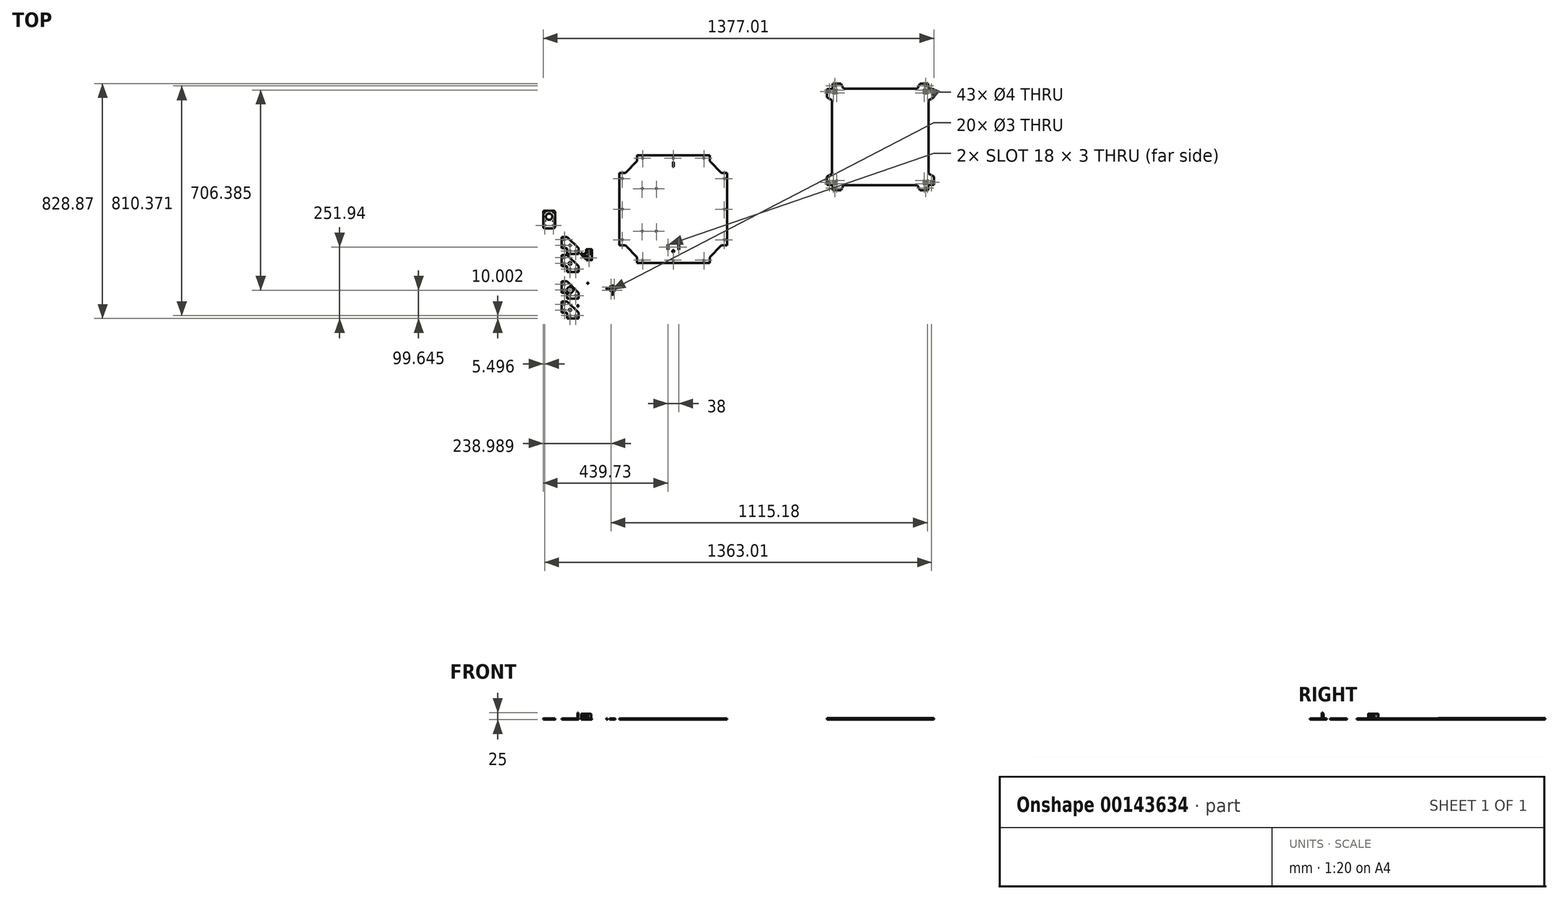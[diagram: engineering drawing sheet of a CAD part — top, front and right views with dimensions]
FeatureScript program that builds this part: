
annotation { "Feature Type Name" : "Feature", "Feature Type Description" : "" }
export const myFeature = defineFeature(function(context is Context, id is Id, definition is map)
    precondition{}
    {
        {
            var Q0;
            Q0=qCreatedBy(makeId("Top.planeOp"),FACE);
            var sketch = newSketch(context, id + "F0", { "sketchPlane" : qUnion([Q0])});
            skLineSegment(sketch, "E0.left", {"start": v(-190, 128) * mm, "end": v(-190, -128) * mm});
            skPoint(sketch, "E0.middle", {"position": v(0, 0) * mm});
            skLineSegment(sketch, "E1", {"start": v(-190, 0) * mm, "end": v(-137.24, 0) * mm, "construction": true});
            skLineSegment(sketch, "E2", {"start": v(0, -170) * mm, "end": v(0, -128) * mm, "construction": true});
            skPoint(sketch, "E3.middle", {"position": v(0, -149) * mm});
            skLineSegment(sketch, "E4", {"start": v(-180, -128) * mm, "end": v(-180, 128) * mm, "construction": true});
            skLineSegment(sketch, "E5", {"start": v(-147, 180) * mm, "end": v(23, 180) * mm, "construction": true});
            skCircle(sketch, "E6", {"center": v(-180, 108) * mm, "radius": 2 * mm});
            skLineSegment(sketch, "E7", {"start": v(23, 180) * mm, "end": v(193, 180) * mm, "construction": true});
            skCircle(sketch, "E8", {"center": v(108, 180) * mm, "radius": 2 * mm});
            skCircle(sketch, "E9.MirrorC", {"center": v(108, -180) * mm, "radius": 2 * mm});
            skLineSegment(sketch, "E10.bottom", {"start": v(-109.57, -77.46) * mm, "end": v(-59.57, -77.46) * mm, "construction": true});
            skLineSegment(sketch, "E10.top", {"start": v(-109.57, 72.54) * mm, "end": v(-59.57, 72.54) * mm, "construction": true});
            skLineSegment(sketch, "E10.left", {"start": v(-109.57, -77.46) * mm, "end": v(-109.57, 72.54) * mm, "construction": true});
            skLineSegment(sketch, "E10.right", {"start": v(-59.57, -77.46) * mm, "end": v(-59.57, 72.54) * mm, "construction": true});
            skCircle(sketch, "E11", {"center": v(-109.57, -77.46) * mm, "radius": 2 * mm});
            skCircle(sketch, "E12", {"center": v(-109.57, 72.54) * mm, "radius": 2 * mm});
            skCircle(sketch, "E13", {"center": v(-59.57, 72.54) * mm, "radius": 2 * mm});
            skCircle(sketch, "E14", {"center": v(-59.57, -77.46) * mm, "radius": 2 * mm});
            skCircle(sketch, "E15", {"center": v(0, -149) * mm, "radius": 3 * mm});
            skLineSegment(sketch, "E16", {"start": v(-373.83, -201.14) * mm, "end": v(-333.84, -161.15) * mm, "construction": true});
            skCircle(sketch, "E17", {"center": v(-363.83, -191.14) * mm, "radius": 11 * mm, "construction": true});
            skCircle(sketch, "E18", {"center": v(-363.83, -191.14) * mm, "radius": 5 * mm});
            skLineSegment(sketch, "E19", {"start": v(-373.83, -181.14) * mm, "end": v(-373.83, -161.14) * mm, "construction": true});
            skPoint(sketch, "E20", {"position": v(-333.83, -201.14) * mm});
            skLineSegment(sketch, "E21", {"start": v(-373.83, -161.14) * mm, "end": v(-393.83, -161.14) * mm});
            skLineSegment(sketch, "E22", {"start": v(-373.83, -161.14) * mm, "end": v(-333.83, -201.14) * mm});
            skLineSegment(sketch, "E23", {"start": v(-383.83, -181.14) * mm, "end": v(-393.83, -181.14) * mm});
            skLineSegment(sketch, "E24", {"start": v(-393.83, -181.14) * mm, "end": v(-373.83, -181.14) * mm});
            skLineSegment(sketch, "E25", {"start": v(-353.83, -201.14) * mm, "end": v(-353.83, -221.14) * mm});
            skLineSegment(sketch, "E26", {"start": v(-393.83, -161.14) * mm, "end": v(-373.83, -181.14) * mm, "construction": true});
            skLineSegment(sketch, "E27", {"start": v(-353.83, -201.14) * mm, "end": v(-333.83, -221.14) * mm, "construction": true});
            skCircle(sketch, "E28", {"center": v(-343.83, -211.14) * mm, "radius": 2 * mm});
            skCircle(sketch, "E29", {"center": v(-383.83, -171.14) * mm, "radius": 2 * mm});
            skCircle(sketch, "E30", {"center": v(-363.83, -191.14) * mm, "radius": 2.5 * mm});
            skLineSegment(sketch, "E31", {"start": v(-333.83, -201.14) * mm, "end": v(-333.83, -221.14) * mm});
            skLineSegment(sketch, "E32", {"start": v(-393.83, -181.14) * mm, "end": v(-393.83, -161.14) * mm});
            skLineSegment(sketch, "E33", {"start": v(-353.83, -221.14) * mm, "end": v(-333.83, -221.14) * mm});
            skLineSegment(sketch, "E34", {"start": v(-373.83, -181.14) * mm, "end": v(-353.83, -201.14) * mm, "construction": true});
            skPoint(sketch, "E35.orphan", {"position": v(-393.82, -221.12) * mm});
            skLineSegment(sketch, "E36", {"start": v(-393.83, -181.14) * mm, "end": v(-393.83, -201.14) * mm});
            skLineSegment(sketch, "E37", {"start": v(-393.83, -201.14) * mm, "end": v(-373.83, -201.14) * mm});
            skLineSegment(sketch, "E38", {"start": v(-373.83, -221.14) * mm, "end": v(-373.83, -201.14) * mm});
            skLineSegment(sketch, "E39", {"start": v(-373.83, -221.14) * mm, "end": v(-353.83, -221.14) * mm});
            skCircle(sketch, "E40.MirrorC", {"center": v(-363.83, -211.14) * mm, "radius": 2 * mm});
            skCircle(sketch, "E41.MirrorC", {"center": v(-383.83, -191.14) * mm, "radius": 2 * mm});
            skCircle(sketch, "E42", {"center": v(-280.98, -260.83) * mm, "radius": 11 * mm, "construction": true});
            skCircle(sketch, "E43", {"center": v(-280.98, -260.83) * mm, "radius": 2.75 * mm});
            skPoint(sketch, "E44", {"position": v(-250.98, -270.83) * mm});
            skLineSegment(sketch, "E45", {"start": v(-300.98, -250.83) * mm, "end": v(-310.98, -250.83) * mm});
            skLineSegment(sketch, "E46", {"start": v(-310.98, -250.83) * mm, "end": v(-270.98, -250.83) * mm});
            skLineSegment(sketch, "E47", {"start": v(-270.98, -250.83) * mm, "end": v(-270.98, -290.83) * mm});
            skLineSegment(sketch, "E48", {"start": v(-290.98, -250.83) * mm, "end": v(-290.98, -270.83) * mm});
            skArc(sketch, "E49", {"start": v(-280.98, -268.83) * mm, "mid": v(-275.33, -255.17) * mm, "end": v(-288.98, -260.83) * mm});
            skLineSegment(sketch, "E50", {"start": v(-290.98, -250.83) * mm, "end": v(-270.98, -270.83) * mm, "construction": true});
            skLineSegment(sketch, "E51", {"start": v(-310.98, -250.83) * mm, "end": v(-310.98, -270.83) * mm});
            skLineSegment(sketch, "E52", {"start": v(-310.98, -270.83) * mm, "end": v(-303.38, -270.83) * mm});
            skLineSegment(sketch, "E53", {"start": v(-290.98, -290.83) * mm, "end": v(-270.98, -290.83) * mm});
            skCircle(sketch, "E54.MirrorC", {"center": v(-280.98, -280.83) * mm, "radius": 2 * mm});
            skCircle(sketch, "E55.MirrorC", {"center": v(-300.98, -260.83) * mm, "radius": 2 * mm});
            skCircle(sketch, "E56.cCircle", {"center": v(-280.98, -260.83) * mm, "radius": 4.75 * mm, "construction": true});
            skLineSegment(sketch, "E56.0", {"start": v(-280.98, -256.08) * mm, "end": v(-276.87, -258.46) * mm});
            skLineSegment(sketch, "E56.1", {"start": v(-276.87, -258.46) * mm, "end": v(-276.87, -263.2) * mm});
            skLineSegment(sketch, "E56.2", {"start": v(-276.87, -263.2) * mm, "end": v(-280.98, -265.58) * mm});
            skLineSegment(sketch, "E56.3", {"start": v(-280.98, -265.58) * mm, "end": v(-285.1, -263.2) * mm});
            skLineSegment(sketch, "E56.4", {"start": v(-285.1, -263.2) * mm, "end": v(-285.1, -258.46) * mm});
            skLineSegment(sketch, "E56.5", {"start": v(-285.1, -258.46) * mm, "end": v(-280.98, -256.08) * mm});
            skLineSegment(sketch, "E57.top", {"start": v(-296.51, -264.83) * mm, "end": v(-292.98, -264.83) * mm});
            skLineSegment(sketch, "E58.left", {"start": v(-284.98, -290.83) * mm, "end": v(-284.98, -283.08) * mm});
            skPoint(sketch, "E59.orphan", {"position": v(-298.73, -264.83) * mm});
            skPoint(sketch, "E60.orphan", {"position": v(-303.23, -264.83) * mm});
            skPoint(sketch, "E61.orphan", {"position": v(-284.98, -278.58) * mm});
            skPoint(sketch, "E62.orphan", {"position": v(-284.98, -283.08) * mm});
            skPoint(sketch, "E63.visualSharp", {"position": v(-287.91, -264.83) * mm});
            skArc(sketch, "E63.filletArc", {"start": v(-292.98, -264.83) * mm, "mid": v(-290.15, -263.66) * mm, "end": v(-288.98, -260.83) * mm});
            skPoint(sketch, "E64.visualSharp", {"position": v(-284.98, -267.76) * mm});
            skArc(sketch, "E64.filletArc", {"start": v(-280.98, -268.83) * mm, "mid": v(-283.81, -270) * mm, "end": v(-284.98, -272.83) * mm});
            skArc(sketch, "E65", {"start": v(-305.46, -264.83) * mm, "mid": v(-300.98, -266.83) * mm, "end": v(-296.51, -264.83) * mm});
            skArc(sketch, "E66", {"start": v(-284.98, -276.36) * mm, "mid": v(-286.98, -280.83) * mm, "end": v(-284.98, -285.3) * mm});
            skLineSegment(sketch, "E67.trimOffspring", {"start": v(-284.98, -278.58) * mm, "end": v(-284.98, -272.83) * mm});
            skLineSegment(sketch, "E68.trimOffspring", {"start": v(-303.23, -264.83) * mm, "end": v(-310.98, -264.83) * mm});
            skLineSegment(sketch, "E69.bottom", {"start": v(559.78, 444.93) * mm, "end": v(899.78, 444.93) * mm});
            skLineSegment(sketch, "E69.top", {"start": v(559.78, 64.93) * mm, "end": v(899.78, 64.93) * mm});
            skLineSegment(sketch, "E69.left", {"start": v(539.78, 424.93) * mm, "end": v(539.78, 84.93) * mm});
            skLineSegment(sketch, "E69.right", {"start": v(919.78, 424.93) * mm, "end": v(919.78, 84.93) * mm});
            skPoint(sketch, "E69.middle", {"position": v(729.78, 254.93) * mm});
            skLineSegment(sketch, "E70.top", {"start": v(539.78, 84.93) * mm, "end": v(559.78, 84.93) * mm});
            skLineSegment(sketch, "E70.right", {"start": v(559.78, 64.93) * mm, "end": v(559.78, 84.93) * mm});
            skLineSegment(sketch, "E71", {"start": v(592.54, 254.93) * mm, "end": v(729.78, 64.93) * mm, "construction": true});
            skLineSegment(sketch, "E72", {"start": v(729.78, 64.93) * mm, "end": v(729.78, 254.93) * mm, "construction": true});
            skLineSegment(sketch, "E73.MirrorCS", {"start": v(559.78, 444.93) * mm, "end": v(559.78, 424.93) * mm});
            skLineSegment(sketch, "E74.MirrorCS", {"start": v(539.78, 424.93) * mm, "end": v(559.78, 424.93) * mm});
            skLineSegment(sketch, "E75.MirrorCS", {"start": v(899.78, 444.93) * mm, "end": v(899.78, 424.93) * mm});
            skLineSegment(sketch, "E76.MirrorCS", {"start": v(919.78, 424.93) * mm, "end": v(899.78, 424.93) * mm});
            skLineSegment(sketch, "E77.MirrorCS", {"start": v(899.78, 64.93) * mm, "end": v(899.78, 84.93) * mm});
            skLineSegment(sketch, "E78.MirrorCS", {"start": v(919.78, 84.93) * mm, "end": v(899.78, 84.93) * mm});
            skLineSegment(sketch, "E79", {"start": v(559.78, 84.93) * mm, "end": v(899.78, 84.93) * mm, "construction": true});
            skLineSegment(sketch, "E80", {"start": v(549.78, 424.93) * mm, "end": v(559.78, 434.93) * mm, "construction": true});
            skLineSegment(sketch, "E81", {"start": v(559.78, 434.93) * mm, "end": v(729.78, 434.93) * mm, "construction": true});
            skLineSegment(sketch, "E82", {"start": v(539.78, 64.93) * mm, "end": v(599.78, 124.93) * mm, "construction": true});
            skCircle(sketch, "E83", {"center": v(569.78, 94.93) * mm, "radius": 11 * mm, "construction": true});
            skCircle(sketch, "E84", {"center": v(569.78, 94.93) * mm, "radius": 4 * mm});
            skCircle(sketch, "E85.MirrorC", {"center": v(569.78, 414.93) * mm, "radius": 2.5 * mm});
            skCircle(sketch, "E86.MirrorC", {"center": v(889.78, 94.93) * mm, "radius": 4 * mm});
            skCircle(sketch, "E87.MirrorC", {"center": v(889.78, 414.93) * mm, "radius": 2.5 * mm});
            skLineSegment(sketch, "E88", {"start": v(559.78, 84.93) * mm, "end": v(559.78, 104.93) * mm, "construction": true});
            skPoint(sketch, "E89", {"position": v(599.78, 84.93) * mm});
            skLineSegment(sketch, "E90", {"start": v(549.78, 104.93) * mm, "end": v(539.78, 104.93) * mm});
            skLineSegment(sketch, "E91", {"start": v(559.78, 84.93) * mm, "end": v(579.78, 84.93) * mm});
            skLineSegment(sketch, "E92", {"start": v(579.78, 84.93) * mm, "end": v(579.78, 64.93) * mm, "construction": true});
            skLineSegment(sketch, "E93", {"start": v(559.78, 104.93) * mm, "end": v(559.78, 84.93) * mm});
            skLineSegment(sketch, "E94", {"start": v(539.78, 124.93) * mm, "end": v(559.78, 104.93) * mm, "construction": true});
            skLineSegment(sketch, "E95", {"start": v(579.78, 84.93) * mm, "end": v(599.78, 64.93) * mm, "construction": true});
            skCircle(sketch, "E96", {"center": v(569.78, 94.93) * mm, "radius": 8 * mm, "construction": true});
            skLineSegment(sketch, "E97", {"start": v(559.78, 104.93) * mm, "end": v(579.78, 84.93) * mm, "construction": true});
            skCircle(sketch, "E98.MirrorC", {"center": v(569.78, 74.93) * mm, "radius": 2 * mm});
            skCircle(sketch, "E99.MirrorC", {"center": v(549.78, 94.93) * mm, "radius": 2 * mm});
            skLineSegment(sketch, "E100", {"start": v(729.78, 254.93) * mm, "end": v(460.72, 254.93) * mm, "construction": true});
            skCircle(sketch, "E101.MirrorC", {"center": v(889.78, 74.93) * mm, "radius": 2 * mm});
            skCircle(sketch, "E102.MirrorC", {"center": v(909.78, 94.93) * mm, "radius": 2 * mm});
            skPoint(sketch, "E103.orphan", {"position": v(539.78, 444.93) * mm});
            skPoint(sketch, "E104.end.orphan", {"position": v(899.78, 434.93) * mm});
            skPoint(sketch, "E105.orphan", {"position": v(919.78, 64.93) * mm});
            skCircle(sketch, "E106.MirrorC", {"center": v(549.78, 414.93) * mm, "radius": 2 * mm});
            skCircle(sketch, "E107.MirrorC", {"center": v(569.78, 434.93) * mm, "radius": 2 * mm});
            skCircle(sketch, "E108.MirrorC", {"center": v(889.78, 434.93) * mm, "radius": 2 * mm});
            skCircle(sketch, "E109.MirrorC", {"center": v(909.78, 414.93) * mm, "radius": 2 * mm});
            skLineSegment(sketch, "E110", {"start": v(-290.98, -270.83) * mm, "end": v(-290.98, -278.43) * mm});
            skLineSegment(sketch, "E111.right", {"start": v(-298.58, -270.83) * mm, "end": v(-298.58, -272.67) * mm});
            skLineSegment(sketch, "E112.MirrorCS", {"start": v(-303.38, -270.83) * mm, "end": v(-303.38, -272.67) * mm});
            skLineSegment(sketch, "E113.bottom", {"start": v(-298.58, -272.67) * mm, "end": v(-297.48, -272.67) * mm});
            skLineSegment(sketch, "E113.right", {"start": v(-297.48, -272.67) * mm, "end": v(-297.48, -275.17) * mm});
            skLineSegment(sketch, "E114.MirrorCS", {"start": v(-304.48, -272.67) * mm, "end": v(-304.48, -275.17) * mm});
            skLineSegment(sketch, "E115.MirrorCS", {"start": v(-303.38, -272.67) * mm, "end": v(-304.48, -272.67) * mm});
            skArc(sketch, "E116", {"start": v(-304.48, -275.17) * mm, "mid": v(-300.98, -275.94) * mm, "end": v(-297.48, -275.17) * mm});
            skLineSegment(sketch, "E117.trimOffspring", {"start": v(-298.58, -270.83) * mm, "end": v(-290.98, -270.83) * mm});
            skPoint(sketch, "E111.bottom.start.orphan", {"position": v(-300.98, -270.83) * mm});
            skLineSegment(sketch, "E118.1.0", {"start": v(-292.82, -237.33) * mm, "end": v(-295.32, -237.33) * mm});
            skLineSegment(sketch, "E118.1.1", {"start": v(-292.82, -244.33) * mm, "end": v(-295.32, -244.33) * mm});
            skLineSegment(sketch, "E118.1.2", {"start": v(-290.98, -238.43) * mm, "end": v(-292.82, -238.43) * mm});
            skArc(sketch, "E118.1.3", {"start": v(-295.32, -237.33) * mm, "mid": v(-296.09, -240.83) * mm, "end": v(-295.32, -244.33) * mm});
            skLineSegment(sketch, "E118.1.4", {"start": v(-290.98, -230.83) * mm, "end": v(-290.98, -238.43) * mm});
            skLineSegment(sketch, "E118.1.5", {"start": v(-290.98, -243.23) * mm, "end": v(-292.82, -243.23) * mm});
            skLineSegment(sketch, "E118.1.6", {"start": v(-292.82, -243.23) * mm, "end": v(-292.82, -244.33) * mm});
            skLineSegment(sketch, "E118.1.7", {"start": v(-292.82, -238.43) * mm, "end": v(-292.82, -237.33) * mm});
            skLineSegment(sketch, "E118.1.8", {"start": v(-290.98, -243.23) * mm, "end": v(-290.98, -250.83) * mm});
            skLineSegment(sketch, "E118.anchor1", {"start": v(-280.98, -260.83) * mm, "end": v(-310.98, -270.83) * mm, "construction": true});
            skLineSegment(sketch, "E118.anchor2", {"start": v(-280.98, -260.83) * mm, "end": v(-290.98, -230.83) * mm, "construction": true});
            skLineSegment(sketch, "E119", {"start": v(-280.98, -260.83) * mm, "end": v(-319.58, -260.83) * mm, "construction": true});
            skPoint(sketch, "E119.endSnap0", {"position": v(-310.98, -260.83) * mm});
            skArc(sketch, "E120.MirrorCS", {"start": v(-295.32, -284.33) * mm, "mid": v(-296.09, -280.83) * mm, "end": v(-295.32, -277.33) * mm});
            skLineSegment(sketch, "E121.MirrorCS", {"start": v(-292.82, -284.33) * mm, "end": v(-295.32, -284.33) * mm});
            skLineSegment(sketch, "E122.MirrorCS", {"start": v(-290.98, -283.23) * mm, "end": v(-292.82, -283.23) * mm});
            skLineSegment(sketch, "E123.MirrorCS", {"start": v(-290.98, -278.43) * mm, "end": v(-292.82, -278.43) * mm});
            skLineSegment(sketch, "E124.MirrorCS", {"start": v(-292.82, -277.33) * mm, "end": v(-295.32, -277.33) * mm});
            skLineSegment(sketch, "E125.MirrorCS", {"start": v(-292.82, -278.43) * mm, "end": v(-292.82, -277.33) * mm});
            skLineSegment(sketch, "E126.MirrorCS", {"start": v(-292.82, -283.23) * mm, "end": v(-292.82, -284.33) * mm});
            skLineSegment(sketch, "E127.trimOffspring", {"start": v(-290.98, -283.23) * mm, "end": v(-290.98, -290.83) * mm});
            skLineSegment(sketch, "E128.0", {"start": v(-297.78, -272.97) * mm, "end": v(-297.78, -275.17) * mm});
            skLineSegment(sketch, "E128.1", {"start": v(-298.88, -272.97) * mm, "end": v(-297.78, -272.97) * mm});
            skLineSegment(sketch, "E128.2", {"start": v(-298.88, -270.83) * mm, "end": v(-298.88, -272.97) * mm});
            skLineSegment(sketch, "E129", {"start": v(-300.98, -270.83) * mm, "end": v(-300.98, -275.04) * mm, "construction": true});
            skLineSegment(sketch, "E130.MirrorCS", {"start": v(-304.18, -272.97) * mm, "end": v(-304.18, -275.17) * mm});
            skLineSegment(sketch, "E131.MirrorCS", {"start": v(-303.08, -270.83) * mm, "end": v(-303.08, -272.97) * mm});
            skLineSegment(sketch, "E132.MirrorCS", {"start": v(-303.08, -272.97) * mm, "end": v(-304.18, -272.97) * mm});
            skArc(sketch, "E133", {"start": v(-304.18, -275.17) * mm, "mid": v(-300.98, -275.98) * mm, "end": v(-297.78, -275.17) * mm});
            skLineSegment(sketch, "E134", {"start": v(-303.38, -270.83) * mm, "end": v(-303.08, -270.83) * mm});
            skLineSegment(sketch, "E135", {"start": v(-298.88, -270.83) * mm, "end": v(-298.58, -270.83) * mm});
            skLineSegment(sketch, "E136", {"start": v(-280.98, -280.83) * mm, "end": v(-291.9, -280.83) * mm, "construction": true});
            skPoint(sketch, "E136.endSnap0", {"position": v(-291.9, -283.23) * mm});
            skLineSegment(sketch, "E137.0", {"start": v(-293.12, -277.63) * mm, "end": v(-295.32, -277.63) * mm});
            skLineSegment(sketch, "E137.1", {"start": v(-293.12, -278.73) * mm, "end": v(-293.12, -277.63) * mm});
            skLineSegment(sketch, "E137.2", {"start": v(-290.98, -278.73) * mm, "end": v(-293.12, -278.73) * mm});
            skLineSegment(sketch, "E138.MirrorCS", {"start": v(-293.12, -284.03) * mm, "end": v(-295.32, -284.03) * mm});
            skLineSegment(sketch, "E139.MirrorCS", {"start": v(-293.12, -282.93) * mm, "end": v(-293.12, -284.03) * mm});
            skLineSegment(sketch, "E140.MirrorCS", {"start": v(-290.98, -282.93) * mm, "end": v(-293.12, -282.93) * mm});
            skArc(sketch, "E141", {"start": v(-295.32, -277.63) * mm, "mid": v(-296.12, -280.83) * mm, "end": v(-295.32, -284.03) * mm});
            skLineSegment(sketch, "E142", {"start": v(-290.98, -278.73) * mm, "end": v(-290.98, -278.43) * mm});
            skLineSegment(sketch, "E143", {"start": v(-290.98, -282.93) * mm, "end": v(-290.98, -283.23) * mm});
            skCircle(sketch, "E144", {"center": v(-214.08, -280.14) * mm, "radius": 11 * mm});
            skCircle(sketch, "E145", {"center": v(-214.08, -280.14) * mm, "radius": 2.75 * mm, "construction": true});
            skPoint(sketch, "E146", {"position": v(-184.08, -290.14) * mm});
            skLineSegment(sketch, "E147", {"start": v(-234.08, -270.14) * mm, "end": v(-244.08, -270.14) * mm});
            skLineSegment(sketch, "E148", {"start": v(-244.08, -270.14) * mm, "end": v(-204.08, -270.14) * mm});
            skLineSegment(sketch, "E149", {"start": v(-204.08, -270.14) * mm, "end": v(-204.08, -310.14) * mm});
            skLineSegment(sketch, "E150", {"start": v(-224.08, -270.14) * mm, "end": v(-204.08, -290.14) * mm, "construction": true});
            skLineSegment(sketch, "E151", {"start": v(-244.08, -270.14) * mm, "end": v(-244.08, -290.14) * mm});
            skLineSegment(sketch, "E152", {"start": v(-244.08, -290.14) * mm, "end": v(-236.48, -290.14) * mm});
            skLineSegment(sketch, "E153", {"start": v(-224.08, -310.14) * mm, "end": v(-204.08, -310.14) * mm});
            skCircle(sketch, "E154.MirrorC", {"center": v(-214.08, -300.14) * mm, "radius": 2 * mm});
            skCircle(sketch, "E155.MirrorC", {"center": v(-234.08, -280.14) * mm, "radius": 2 * mm});
            skCircle(sketch, "E156.cCircle", {"center": v(-214.08, -280.14) * mm, "radius": 4.75 * mm, "construction": true});
            skLineSegment(sketch, "E156.0", {"start": v(-214.08, -275.39) * mm, "end": v(-209.97, -277.76) * mm, "construction": true});
            skLineSegment(sketch, "E156.1", {"start": v(-209.97, -277.76) * mm, "end": v(-209.97, -282.51) * mm, "construction": true});
            skLineSegment(sketch, "E156.2", {"start": v(-209.97, -282.51) * mm, "end": v(-214.08, -284.89) * mm, "construction": true});
            skLineSegment(sketch, "E156.3", {"start": v(-214.08, -284.89) * mm, "end": v(-218.2, -282.51) * mm, "construction": true});
            skLineSegment(sketch, "E156.4", {"start": v(-218.2, -282.51) * mm, "end": v(-218.2, -277.76) * mm, "construction": true});
            skLineSegment(sketch, "E156.5", {"start": v(-218.2, -277.76) * mm, "end": v(-214.08, -275.39) * mm, "construction": true});
            skLineSegment(sketch, "E157.top", {"start": v(-229.61, -284.14) * mm, "end": v(-224.33, -284.14) * mm});
            skLineSegment(sketch, "E158.left", {"start": v(-218.08, -310.14) * mm, "end": v(-218.08, -302.39) * mm});
            skPoint(sketch, "E159.orphan", {"position": v(-231.83, -284.14) * mm});
            skPoint(sketch, "E160.orphan", {"position": v(-236.33, -284.14) * mm});
            skPoint(sketch, "E161.orphan", {"position": v(-218.08, -297.89) * mm});
            skPoint(sketch, "E162.orphan", {"position": v(-218.08, -302.39) * mm});
            skPoint(sketch, "E163.visualSharp", {"position": v(-221.01, -284.14) * mm});
            skPoint(sketch, "E164.visualSharp", {"position": v(-218.08, -287.07) * mm});
            skArc(sketch, "E165", {"start": v(-238.56, -284.14) * mm, "mid": v(-234.08, -286.14) * mm, "end": v(-229.61, -284.14) * mm});
            skArc(sketch, "E166", {"start": v(-218.08, -295.67) * mm, "mid": v(-220.08, -300.14) * mm, "end": v(-218.08, -304.61) * mm});
            skLineSegment(sketch, "E167.trimOffspring", {"start": v(-218.08, -297.89) * mm, "end": v(-218.08, -290.39) * mm});
            skLineSegment(sketch, "E168.trimOffspring", {"start": v(-236.33, -284.14) * mm, "end": v(-244.08, -284.14) * mm});
            skLineSegment(sketch, "E169", {"start": v(-224.08, -290.14) * mm, "end": v(-224.08, -297.74) * mm});
            skLineSegment(sketch, "E170.right", {"start": v(-231.68, -290.14) * mm, "end": v(-231.68, -291.98) * mm});
            skLineSegment(sketch, "E171.MirrorCS", {"start": v(-236.48, -290.14) * mm, "end": v(-236.48, -291.98) * mm});
            skLineSegment(sketch, "E172.bottom", {"start": v(-231.68, -291.98) * mm, "end": v(-230.58, -291.98) * mm});
            skLineSegment(sketch, "E172.right", {"start": v(-230.58, -291.98) * mm, "end": v(-230.58, -294.48) * mm});
            skLineSegment(sketch, "E173.MirrorCS", {"start": v(-237.58, -291.98) * mm, "end": v(-237.58, -294.48) * mm});
            skLineSegment(sketch, "E174.MirrorCS", {"start": v(-236.48, -291.98) * mm, "end": v(-237.58, -291.98) * mm});
            skArc(sketch, "E175", {"start": v(-237.58, -294.48) * mm, "mid": v(-234.08, -295.24) * mm, "end": v(-230.58, -294.48) * mm});
            skLineSegment(sketch, "E176.trimOffspring", {"start": v(-231.68, -290.14) * mm, "end": v(-224.08, -290.14) * mm});
            skPoint(sketch, "E170.bottom.start.orphan", {"position": v(-234.08, -290.14) * mm});
            skLineSegment(sketch, "E177.1.0", {"start": v(-225.92, -256.64) * mm, "end": v(-228.42, -256.64) * mm});
            skLineSegment(sketch, "E177.1.1", {"start": v(-225.92, -263.64) * mm, "end": v(-228.42, -263.64) * mm});
            skLineSegment(sketch, "E177.1.2", {"start": v(-224.08, -257.74) * mm, "end": v(-225.92, -257.74) * mm});
            skArc(sketch, "E177.1.3", {"start": v(-228.42, -256.64) * mm, "mid": v(-229.2, -260.14) * mm, "end": v(-228.42, -263.64) * mm});
            skLineSegment(sketch, "E177.1.4", {"start": v(-224.08, -250.14) * mm, "end": v(-224.08, -257.74) * mm});
            skLineSegment(sketch, "E177.1.5", {"start": v(-224.08, -262.54) * mm, "end": v(-225.92, -262.54) * mm});
            skLineSegment(sketch, "E177.1.6", {"start": v(-225.92, -262.54) * mm, "end": v(-225.92, -263.64) * mm});
            skLineSegment(sketch, "E177.1.7", {"start": v(-225.92, -257.74) * mm, "end": v(-225.92, -256.64) * mm});
            skLineSegment(sketch, "E177.1.8", {"start": v(-224.08, -262.54) * mm, "end": v(-224.08, -270.14) * mm});
            skLineSegment(sketch, "E177.anchor1", {"start": v(-214.08, -280.14) * mm, "end": v(-244.08, -290.14) * mm, "construction": true});
            skLineSegment(sketch, "E177.anchor2", {"start": v(-214.08, -280.14) * mm, "end": v(-224.08, -250.14) * mm, "construction": true});
            skLineSegment(sketch, "E178", {"start": v(-214.08, -280.14) * mm, "end": v(-252.68, -280.14) * mm, "construction": true});
            skPoint(sketch, "E178.endSnap0", {"position": v(-244.08, -280.14) * mm});
            skArc(sketch, "E179.MirrorCS", {"start": v(-228.42, -303.64) * mm, "mid": v(-229.2, -300.14) * mm, "end": v(-228.42, -296.64) * mm});
            skLineSegment(sketch, "E180.MirrorCS", {"start": v(-225.92, -303.64) * mm, "end": v(-228.42, -303.64) * mm});
            skLineSegment(sketch, "E181.MirrorCS", {"start": v(-224.08, -302.54) * mm, "end": v(-225.92, -302.54) * mm});
            skLineSegment(sketch, "E182.MirrorCS", {"start": v(-224.08, -297.74) * mm, "end": v(-225.92, -297.74) * mm});
            skLineSegment(sketch, "E183.MirrorCS", {"start": v(-225.92, -296.64) * mm, "end": v(-228.42, -296.64) * mm});
            skLineSegment(sketch, "E184.MirrorCS", {"start": v(-225.92, -297.74) * mm, "end": v(-225.92, -296.64) * mm});
            skLineSegment(sketch, "E185.MirrorCS", {"start": v(-225.92, -302.54) * mm, "end": v(-225.92, -303.64) * mm});
            skLineSegment(sketch, "E186.trimOffspring", {"start": v(-224.08, -302.54) * mm, "end": v(-224.08, -310.14) * mm});
            skLineSegment(sketch, "E187.0", {"start": v(-230.88, -292.28) * mm, "end": v(-230.88, -294.48) * mm});
            skLineSegment(sketch, "E187.1", {"start": v(-231.98, -292.28) * mm, "end": v(-230.88, -292.28) * mm});
            skLineSegment(sketch, "E187.2", {"start": v(-231.98, -290.14) * mm, "end": v(-231.98, -292.28) * mm});
            skLineSegment(sketch, "E188", {"start": v(-234.08, -290.14) * mm, "end": v(-234.08, -294.35) * mm, "construction": true});
            skLineSegment(sketch, "E189.MirrorCS", {"start": v(-237.28, -292.28) * mm, "end": v(-237.28, -294.48) * mm});
            skLineSegment(sketch, "E190.MirrorCS", {"start": v(-236.18, -290.14) * mm, "end": v(-236.18, -292.28) * mm});
            skLineSegment(sketch, "E191.MirrorCS", {"start": v(-236.18, -292.28) * mm, "end": v(-237.28, -292.28) * mm});
            skArc(sketch, "E192", {"start": v(-237.28, -294.48) * mm, "mid": v(-234.08, -295.3) * mm, "end": v(-230.88, -294.48) * mm});
            skLineSegment(sketch, "E193", {"start": v(-236.48, -290.14) * mm, "end": v(-236.18, -290.14) * mm});
            skLineSegment(sketch, "E194", {"start": v(-231.98, -290.14) * mm, "end": v(-231.68, -290.14) * mm});
            skLineSegment(sketch, "E195", {"start": v(-214.08, -300.14) * mm, "end": v(-225, -300.14) * mm, "construction": true});
            skPoint(sketch, "E195.endSnap0", {"position": v(-225, -302.54) * mm});
            skLineSegment(sketch, "E196.0", {"start": v(-226.22, -296.94) * mm, "end": v(-228.42, -296.94) * mm});
            skLineSegment(sketch, "E196.1", {"start": v(-226.22, -298.04) * mm, "end": v(-226.22, -296.94) * mm});
            skLineSegment(sketch, "E196.2", {"start": v(-224.08, -298.04) * mm, "end": v(-226.22, -298.04) * mm});
            skLineSegment(sketch, "E197.MirrorCS", {"start": v(-226.22, -303.34) * mm, "end": v(-228.42, -303.34) * mm});
            skLineSegment(sketch, "E198.MirrorCS", {"start": v(-226.22, -302.24) * mm, "end": v(-226.22, -303.34) * mm});
            skLineSegment(sketch, "E199.MirrorCS", {"start": v(-224.08, -302.24) * mm, "end": v(-226.22, -302.24) * mm});
            skArc(sketch, "E200", {"start": v(-228.42, -296.94) * mm, "mid": v(-229.23, -300.14) * mm, "end": v(-228.42, -303.34) * mm});
            skLineSegment(sketch, "E201", {"start": v(-224.08, -298.04) * mm, "end": v(-224.08, -297.74) * mm});
            skLineSegment(sketch, "E202", {"start": v(-224.08, -302.24) * mm, "end": v(-224.08, -302.54) * mm});
            skCircle(sketch, "E203", {"center": v(-214.08, -280.14) * mm, "radius": 8 * mm, "construction": true});
            skCircle(sketch, "E204", {"center": v(-214.08, -280.14) * mm, "radius": 5.1 * mm});
            skCircle(sketch, "E205", {"center": v(-219.74, -274.48) * mm, "radius": 1.5 * mm});
            skCircle(sketch, "E206.1.0", {"center": v(-219.74, -285.8) * mm, "radius": 1.5 * mm});
            skCircle(sketch, "E206.2.0", {"center": v(-208.43, -285.8) * mm, "radius": 1.5 * mm});
            skCircle(sketch, "E206.3.0", {"center": v(-208.43, -274.48) * mm, "radius": 1.5 * mm});
            skCircle(sketch, "E207", {"center": v(564.12, 100.59) * mm, "radius": 1.5 * mm});
            skLineSegment(sketch, "E208", {"start": v(569.78, 94.93) * mm, "end": v(580.78, 94.93) * mm, "construction": true});
            skCircle(sketch, "E209.MirrorC", {"center": v(564.12, 89.28) * mm, "radius": 1.5 * mm});
            skLineSegment(sketch, "E210", {"start": v(569.78, 94.93) * mm, "end": v(569.78, 69.23) * mm, "construction": true});
            skCircle(sketch, "E211.MirrorC", {"center": v(575.43, 89.28) * mm, "radius": 1.5 * mm});
            skCircle(sketch, "E212.MirrorC", {"center": v(575.43, 100.59) * mm, "radius": 1.5 * mm});
            skCircle(sketch, "E213.MirrorC", {"center": v(895.43, 100.59) * mm, "radius": 1.5 * mm});
            skCircle(sketch, "E214.MirrorC", {"center": v(884.12, 100.59) * mm, "radius": 1.5 * mm});
            skCircle(sketch, "E215.MirrorC", {"center": v(895.43, 89.28) * mm, "radius": 1.5 * mm});
            skCircle(sketch, "E216.MirrorC", {"center": v(884.12, 89.28) * mm, "radius": 1.5 * mm});
            skCircle(sketch, "E217.MirrorC", {"center": v(564.12, 420.59) * mm, "radius": 1.5 * mm});
            skCircle(sketch, "E218.MirrorC", {"center": v(564.12, 409.28) * mm, "radius": 1.5 * mm});
            skCircle(sketch, "E219.MirrorC", {"center": v(575.43, 409.28) * mm, "radius": 1.5 * mm});
            skCircle(sketch, "E220.MirrorC", {"center": v(575.43, 420.59) * mm, "radius": 1.5 * mm});
            skCircle(sketch, "E221.MirrorC", {"center": v(895.43, 409.28) * mm, "radius": 1.5 * mm});
            skCircle(sketch, "E222.MirrorC", {"center": v(884.12, 409.28) * mm, "radius": 1.5 * mm});
            skCircle(sketch, "E223.MirrorC", {"center": v(884.12, 420.59) * mm, "radius": 1.5 * mm});
            skCircle(sketch, "E224.MirrorC", {"center": v(895.43, 420.59) * mm, "radius": 1.5 * mm});
            skPoint(sketch, "E225.orphan", {"position": v(919.78, 444.93) * mm});
            skLineSegment(sketch, "E226.0", {"start": v(561.28, 443.43) * mm, "end": v(561.28, 423.43) * mm});
            skLineSegment(sketch, "E226.1", {"start": v(918.28, 86.43) * mm, "end": v(898.28, 86.43) * mm});
            skLineSegment(sketch, "E226.2", {"start": v(918.28, 423.43) * mm, "end": v(918.28, 86.43) * mm});
            skLineSegment(sketch, "E226.3", {"start": v(918.28, 423.43) * mm, "end": v(898.28, 423.43) * mm});
            skLineSegment(sketch, "E226.4", {"start": v(898.28, 443.43) * mm, "end": v(898.28, 423.43) * mm});
            skLineSegment(sketch, "E226.5", {"start": v(898.28, 66.43) * mm, "end": v(898.28, 86.43) * mm});
            skLineSegment(sketch, "E226.6", {"start": v(561.28, 443.43) * mm, "end": v(898.28, 443.43) * mm});
            skLineSegment(sketch, "E226.7", {"start": v(561.28, 66.43) * mm, "end": v(898.28, 66.43) * mm});
            skLineSegment(sketch, "E226.8", {"start": v(561.28, 66.43) * mm, "end": v(561.28, 86.43) * mm});
            skLineSegment(sketch, "E226.9", {"start": v(541.28, 86.43) * mm, "end": v(561.28, 86.43) * mm});
            skLineSegment(sketch, "E226.10", {"start": v(541.28, 423.43) * mm, "end": v(541.28, 86.43) * mm});
            skLineSegment(sketch, "E226.11", {"start": v(541.28, 423.43) * mm, "end": v(561.28, 423.43) * mm});
            skPoint(sketch, "E227", {"position": v(-43, -190) * mm});
            skCircle(sketch, "E228", {"center": v(-19, -141) * mm, "radius": 1.5 * mm});
            skCircle(sketch, "E229.MirrorC", {"center": v(19, -141) * mm, "radius": 1.5 * mm});
            skLineSegment(sketch, "E230.0", {"start": v(-128, -169.17) * mm, "end": v(-128, -190) * mm});
            skLineSegment(sketch, "E230.1", {"start": v(-169.17, -128) * mm, "end": v(-128, -169.17) * mm});
            skLineSegment(sketch, "E230.2", {"start": v(-190, -128) * mm, "end": v(-169.17, -128) * mm});
            skLineSegment(sketch, "E231.MirrorCS", {"start": v(169.17, -128) * mm, "end": v(128, -169.17) * mm});
            skLineSegment(sketch, "E232.MirrorCS", {"start": v(190, -128) * mm, "end": v(169.17, -128) * mm});
            skLineSegment(sketch, "E233.MirrorCS", {"start": v(128, -169.17) * mm, "end": v(128, -190) * mm});
            skLineSegment(sketch, "E234.MirrorCS", {"start": v(-169.17, 128) * mm, "end": v(-128, 169.17) * mm});
            skLineSegment(sketch, "E235.MirrorCS", {"start": v(190, 128) * mm, "end": v(169.17, 128) * mm});
            skLineSegment(sketch, "E236.MirrorCS", {"start": v(169.17, 128) * mm, "end": v(128, 169.17) * mm});
            skLineSegment(sketch, "E237.MirrorCS", {"start": v(128, 169.17) * mm, "end": v(128, 190) * mm});
            skLineSegment(sketch, "E238.MirrorCS", {"start": v(-128, 169.17) * mm, "end": v(-128, 190) * mm});
            skLineSegment(sketch, "E239.MirrorCS", {"start": v(-190, 128) * mm, "end": v(-169.17, 128) * mm});
            skLineSegment(sketch, "E240.trimOffspring", {"start": v(-128, 190) * mm, "end": v(128, 190) * mm});
            skLineSegment(sketch, "E241.trimOffspring", {"start": v(190, 128) * mm, "end": v(190, -128) * mm});
            skLineSegment(sketch, "E242.trimOffspring", {"start": v(-128, -190) * mm, "end": v(128, -190) * mm});
            skCircle(sketch, "E243.0.1.0", {"center": v(0, -147.5) * mm, "radius": 3 * mm});
            skLineSegment(sketch, "E243.direction1", {"start": v(0, -149) * mm, "end": v(25, -149) * mm, "construction": true});
            skLineSegment(sketch, "E243.direction2", {"start": v(0, -149) * mm, "end": v(0, -147.5) * mm, "construction": true});
            skLineSegment(sketch, "E244", {"start": v(-3, -149.18) * mm, "end": v(-3, -147.5) * mm});
            skLineSegment(sketch, "E245", {"start": v(3, -149) * mm, "end": v(3, -147.5) * mm});
            skCircle(sketch, "E246", {"center": v(0, -180) * mm, "radius": 2 * mm});
            skCircle(sketch, "E247.MirrorC", {"center": v(-108, -180) * mm, "radius": 2 * mm});
            skCircle(sketch, "E248.MirrorC", {"center": v(-108, 180) * mm, "radius": 2 * mm});
            skCircle(sketch, "E249", {"center": v(0, 180) * mm, "radius": 2 * mm});
            skCircle(sketch, "E250.MirrorC", {"center": v(-180, -108) * mm, "radius": 2 * mm});
            skCircle(sketch, "E251", {"center": v(-180, 0) * mm, "radius": 2 * mm});
            skCircle(sketch, "E252.MirrorC", {"center": v(180, -108) * mm, "radius": 2 * mm});
            skCircle(sketch, "E253.MirrorC", {"center": v(180, 0) * mm, "radius": 2 * mm});
            skCircle(sketch, "E254.MirrorC", {"center": v(180, 108) * mm, "radius": 2 * mm});
            skCircle(sketch, "E255", {"center": v(-363.83, -191.14) * mm, "radius": 4 * mm});
            skCircle(sketch, "E256", {"center": v(-363.83, -191.14) * mm, "radius": 11 * mm});
            skLineSegment(sketch, "E257.bottom", {"start": v(-421.73, -5.25) * mm, "end": v(-453.73, -5.25) * mm});
            skLineSegment(sketch, "E257.left", {"start": v(-416.73, -10.25) * mm, "end": v(-416.73, -47.25) * mm});
            skLineSegment(sketch, "E257.right", {"start": v(-458.73, -10.25) * mm, "end": v(-458.73, -47.25) * mm});
            skPoint(sketch, "E257.middle", {"position": v(-437.73, -26.25) * mm});
            skLineSegment(sketch, "E258.left", {"start": v(-458.73, -47.25) * mm, "end": v(-458.73, -47.25) * mm});
            skLineSegment(sketch, "E258.right", {"start": v(-416.73, -47.25) * mm, "end": v(-416.73, -47.25) * mm});
            skLineSegment(sketch, "E259.left", {"start": v(-458.73, -47.25) * mm, "end": v(-458.73, -62.25) * mm});
            skLineSegment(sketch, "E259.right", {"start": v(-416.73, -47.25) * mm, "end": v(-416.73, -62.25) * mm});
            skLineSegment(sketch, "E260", {"start": v(-453.73, -67.25) * mm, "end": v(-421.73, -67.25) * mm});
            skCircle(sketch, "E261", {"center": v(-437.73, -26.25) * mm, "radius": 11.25 * mm});
            skLineSegment(sketch, "E262.bottom", {"start": v(-422.23, -10.75) * mm, "end": v(-453.23, -10.75) * mm, "construction": true});
            skLineSegment(sketch, "E262.top", {"start": v(-422.23, -41.75) * mm, "end": v(-453.23, -41.75) * mm, "construction": true});
            skLineSegment(sketch, "E262.left", {"start": v(-422.23, -10.75) * mm, "end": v(-422.23, -41.75) * mm, "construction": true});
            skLineSegment(sketch, "E262.right", {"start": v(-453.23, -10.75) * mm, "end": v(-453.23, -41.75) * mm, "construction": true});
            skLineSegment(sketch, "E263", {"start": v(-458.73, -57.25) * mm, "end": v(-416.73, -57.25) * mm, "construction": true});
            skCircle(sketch, "E264", {"center": v(-453.23, -57.25) * mm, "radius": 2 * mm});
            skCircle(sketch, "E265", {"center": v(-422.23, -57.25) * mm, "radius": 2 * mm});
            skCircle(sketch, "E266", {"center": v(-453.23, -10.75) * mm, "radius": 1.55 * mm});
            skCircle(sketch, "E267", {"center": v(-422.23, -10.75) * mm, "radius": 1.55 * mm});
            skCircle(sketch, "E268", {"center": v(-422.23, -41.75) * mm, "radius": 1.55 * mm});
            skCircle(sketch, "E269", {"center": v(-453.23, -41.75) * mm, "radius": 1.55 * mm});
            skPoint(sketch, "E270.visualSharp", {"position": v(-458.73, -5.25) * mm});
            skArc(sketch, "E270.filletArc", {"start": v(-453.73, -5.25) * mm, "mid": v(-457.27, -6.71) * mm, "end": v(-458.73, -10.25) * mm});
            skPoint(sketch, "E271.visualSharp", {"position": v(-416.73, -5.25) * mm});
            skArc(sketch, "E271.filletArc", {"start": v(-416.73, -10.25) * mm, "mid": v(-418.2, -6.71) * mm, "end": v(-421.73, -5.25) * mm});
            skPoint(sketch, "E272.visualSharp", {"position": v(-458.73, -67.25) * mm});
            skArc(sketch, "E272.filletArc", {"start": v(-458.73, -62.25) * mm, "mid": v(-457.27, -65.78) * mm, "end": v(-453.73, -67.25) * mm});
            skPoint(sketch, "E273.visualSharp", {"position": v(-416.73, -67.25) * mm});
            skArc(sketch, "E273.filletArc", {"start": v(-421.73, -67.25) * mm, "mid": v(-418.2, -65.78) * mm, "end": v(-416.73, -62.25) * mm});
            skLineSegment(sketch, "E274", {"start": v(589.78, 64.93) * mm, "end": v(599.78, 84.93) * mm});
            skPoint(sketch, "E274.startSnap0", {"position": v(589.78, 74.93) * mm});
            skLineSegment(sketch, "E275", {"start": v(539.78, 114.93) * mm, "end": v(559.78, 124.93) * mm});
            skPoint(sketch, "E275.startSnap0", {"position": v(549.78, 114.93) * mm});
            skLineSegment(sketch, "E276.MirrorCS", {"start": v(539.78, 394.93) * mm, "end": v(559.78, 384.93) * mm});
            skLineSegment(sketch, "E277.MirrorCS", {"start": v(589.78, 444.93) * mm, "end": v(599.78, 424.93) * mm});
            skLineSegment(sketch, "E278.MirrorCS", {"start": v(869.78, 64.93) * mm, "end": v(859.78, 84.93) * mm});
            skLineSegment(sketch, "E279.MirrorCS", {"start": v(919.78, 114.93) * mm, "end": v(899.78, 124.93) * mm});
            skLineSegment(sketch, "E280.MirrorCS", {"start": v(919.78, 394.93) * mm, "end": v(899.78, 384.93) * mm});
            skLineSegment(sketch, "E281.MirrorCS", {"start": v(869.78, 444.93) * mm, "end": v(859.78, 424.93) * mm});
            skLineSegment(sketch, "E282", {"start": v(599.78, 424.93) * mm, "end": v(859.78, 424.93) * mm});
            skLineSegment(sketch, "E283", {"start": v(559.78, 384.93) * mm, "end": v(559.78, 124.93) * mm});
            skLineSegment(sketch, "E284", {"start": v(859.78, 84.93) * mm, "end": v(599.78, 84.93) * mm});
            skLineSegment(sketch, "E285", {"start": v(899.78, 124.93) * mm, "end": v(899.78, 384.93) * mm});
            skLineSegment(sketch, "E286.0", {"start": v(-308.98, -250.83) * mm, "end": v(-308.98, -270.83) * mm});
            skLineSegment(sketch, "E287.0", {"start": v(-290.98, -288.83) * mm, "end": v(-270.98, -288.83) * mm});
            skLineSegment(sketch, "E288.0", {"start": v(-242.08, -270.14) * mm, "end": v(-242.08, -290.14) * mm});
            skLineSegment(sketch, "E289.0", {"start": v(-224.08, -308.14) * mm, "end": v(-204.08, -308.14) * mm});
            skLineSegment(sketch, "E290", {"start": v(-19, -141) * mm, "end": v(19, -141) * mm, "construction": true});
            skLineSegment(sketch, "E291", {"start": v(0, -141) * mm, "end": v(0, -128) * mm, "construction": true});
            skCircle(sketch, "E292.0.1.0", {"center": v(-19, -126) * mm, "radius": 1.5 * mm});
            skCircle(sketch, "E292.0.1.1", {"center": v(19, -126) * mm, "radius": 1.5 * mm});
            skLineSegment(sketch, "E292.direction1", {"start": v(-19, -141) * mm, "end": v(4, -141) * mm, "construction": true});
            skLineSegment(sketch, "E292.direction2", {"start": v(-19, -141) * mm, "end": v(-19, -126) * mm, "construction": true});
            skLineSegment(sketch, "E293", {"start": v(-20.5, -141) * mm, "end": v(-20.5, -126) * mm});
            skLineSegment(sketch, "E294", {"start": v(-17.5, -126) * mm, "end": v(-17.5, -141) * mm});
            skLineSegment(sketch, "E295", {"start": v(17.5, -126) * mm, "end": v(17.5, -141) * mm});
            skLineSegment(sketch, "E296", {"start": v(20.5, -141) * mm, "end": v(20.5, -126) * mm});
            skCircle(sketch, "E297.MirrorC", {"center": v(0, 151) * mm, "radius": 1.5 * mm});
            skCircle(sketch, "E298.0.1.1", {"center": v(0, 165) * mm, "radius": 1.5 * mm});
            skLineSegment(sketch, "E299", {"start": v(-1.5, 165) * mm, "end": v(-1.5, 151) * mm});
            skLineSegment(sketch, "E300", {"start": v(1.5, 151) * mm, "end": v(1.5, 165) * mm});
            skPoint(sketch, "E301.endSnap0", {"position": v(0, 190) * mm});
            skLineSegment(sketch, "E302", {"start": v(0, 165) * mm, "end": v(0, 190) * mm, "construction": true});
            skSolve(sketch);
        }
        {
            var Q0;
            Q0=makeQuery(id+"F0.imprint","IMPRINT",FACE,{"disambiguationData":[TD([[makeQuery(id+"F0.imprint","IMPRINT",EDGE,{"derivedFrom":sQuery(id+"F0.wireOp",EDGE,"E0.left")}),1.0]])]});
            var Q1;
            Q1=makeQuery(id+"F0.imprint","IMPRINT",FACE,{"disambiguationData":[TD([[makeQuery(id+"F0.imprint","IMPRINT",EDGE,{"derivedFrom":sQuery(id+"F0.wireOp",EDGE,"E257.bottom")}),1.0]])]});
            extrude(context, id + "F1", {"entities" : qUnion([Q0, Q1]), "depth" : 4 * mm});
        }
        {
            var Q0;
            Q0=makeQuery(id+"F0.imprint","IMPRINT",FACE,{"disambiguationData":[TD([[makeQuery(id+"F0.imprint","IMPRINT",EDGE,{"derivedFrom":sQuery(id+"F0.wireOp",EDGE,"E21")}),1.0]])]});
            var Q1;
            {var subQ1=sQuery(id+"F0.wireOp",EDGE,"c733202e-df79-4c57-a5cb-e2746a1ac155");Q1=makeQuery(id+"F0.imprint","IMPRINT",FACE,{"disambiguationData":[TD([[makeQuery(id+"F0.imprint","IMPRINT",EDGE,{"derivedFrom":subQ1}),-1.0]])]});}
            var Q2;
            Q2=makeQuery(id+"F0.imprint","IMPRINT",FACE,{"disambiguationData":[TD([[makeQuery(id+"F0.imprint","IMPRINT",EDGE,{"derivedFrom":sQuery(id+"F0.wireOp",EDGE,"f4d605e5-f8c4-4358-9a59-65ac05495e07")}),-1.0]])]});
            var Q3;
            Q3=makeQuery(id+"F0.imprint","IMPRINT",FACE,{"disambiguationData":[TD([[makeQuery(id+"F0.imprint","IMPRINT",EDGE,{"derivedFrom":sQuery(id+"F0.wireOp",EDGE,"E18")}),-1.0]])]});
            extrude(context, id + "F2", {"entities" : qUnion([Q0, Q1, Q2, Q3]), "depth" : 4 * mm});
        }
        {
            var Q0;
            Q0=makeQuery(id+"F0.imprint","IMPRINT",FACE,{"disambiguationData":[TD([[makeQuery(id+"F0.imprint","IMPRINT",EDGE,{"derivedFrom":sQuery(id+"F0.wireOp",EDGE,"E21")}),1.0]])]});
            var Q1;
            {var subQ1=sQuery(id+"F0.wireOp",EDGE,"c733202e-df79-4c57-a5cb-e2746a1ac155");Q1=makeQuery(id+"F0.imprint","IMPRINT",FACE,{"disambiguationData":[TD([[makeQuery(id+"F0.imprint","IMPRINT",EDGE,{"derivedFrom":subQ1}),-1.0]])]});}
            var Q2;
            Q2=makeQuery(id+"F0.imprint","IMPRINT",FACE,{"disambiguationData":[TD([[makeQuery(id+"F0.imprint","IMPRINT",EDGE,{"derivedFrom":sQuery(id+"F0.wireOp",EDGE,"f4d605e5-f8c4-4358-9a59-65ac05495e07")}),-1.0]])]});
            var Q3;
            Q3=makeQuery(id+"F0.imprint","IMPRINT",FACE,{"disambiguationData":[TD([[makeQuery(id+"F0.imprint","IMPRINT",EDGE,{"derivedFrom":sQuery(id+"F0.wireOp",EDGE,"E18")}),1.0]])]});
            var Q4;
            Q4=makeQuery(id+"F0.imprint","IMPRINT",FACE,{"disambiguationData":[TD([[makeQuery(id+"F0.imprint","IMPRINT",EDGE,{"derivedFrom":sQuery(id+"F0.wireOp",EDGE,"E18")}),-1.0]])]});
            var Q5;
            Q5=makeQuery(id+"F0.imprint","IMPRINT",FACE,{"disambiguationData":[TD([[makeQuery(id+"F0.imprint","IMPRINT",EDGE,{"derivedFrom":sQuery(id+"F0.wireOp",EDGE,"E30")}),-1.0]])]});
            extrude(context, id + "F3", {"entities" : qUnion([Q0, Q1, Q2, Q3, Q4, Q5]), "depth" : 4 * mm});
        }
        {
            var Q0;
            {var subQ5=sQuery(id+"F0.wireOp",EDGE,"ckVaXHjw-fDKv-VBhn-iOhb-UEGDB8ZxVIm3");Q0=makeQuery(id+"F0.imprint","IMPRINT",FACE,{"disambiguationData":[TD([[makeQuery(id+"F0.imprint","IMPRINT",EDGE,{"derivedFrom":subQ5}),-1.0]])]});}
            var Q1;
            {var subQ11=sQuery(id+"F0.wireOp",EDGE,"E57.top");Q1=makeQuery(id+"F0.imprint","IMPRINT",FACE,{"disambiguationData":[TD([[makeQuery(id+"F0.imprint","IMPRINT",EDGE,{"derivedFrom":subQ11}),-1.0]])]});}
            var Q2;
            {var subQ11=sQuery(id+"F0.wireOp",EDGE,"E49");Q2=makeQuery(id+"F0.imprint","IMPRINT",FACE,{"disambiguationData":[TD([[makeQuery(id+"F0.imprint","IMPRINT",EDGE,{"derivedFrom":subQ11}),1.0]])]});}
            var Q3;
            {var subQ11=sQuery(id+"F0.wireOp",EDGE,"E49");Q3=makeQuery(id+"F0.imprint","IMPRINT",FACE,{"disambiguationData":[TD([[makeQuery(id+"F0.imprint","IMPRINT",EDGE,{"derivedFrom":subQ11}),1.0]])]});}
            var Q4;
            {var subQ5=sQuery(id+"F0.wireOp",EDGE,"p1GlZLba-3Vl4-jr42-5wS3-6L51oModQ6wH");Q4=makeQuery(id+"F0.imprint","IMPRINT",FACE,{"disambiguationData":[TD([[makeQuery(id+"F0.imprint","IMPRINT",EDGE,{"derivedFrom":subQ5}),1.0]])]});}
            extrude(context, id + "F4", {"entities" : qUnion([Q0, Q1, Q2, Q3, Q4]), "depth" : 21 * mm});
        }
        {
            var Q0;
            Q0=makeQuery(id+"F0.imprint","IMPRINT",FACE,{"disambiguationData":[TD([[makeQuery(id+"F0.imprint","IMPRINT",EDGE,{"derivedFrom":sQuery(id+"F0.wireOp",EDGE,"E55.MirrorC")}),1.0]])]});
            var Q1;
            {var subQ7=sQuery(id+"F0.wireOp",EDGE,"d21323fb-2d8b-4c74-bdcf-1873a6e3dc00");Q1=makeQuery(id+"F0.imprint","IMPRINT",FACE,{"disambiguationData":[TD([[makeQuery(id+"F0.imprint","IMPRINT",EDGE,{"derivedFrom":subQ7}),1.0]])]});}
            var Q2;
            {var subQ1=sQuery(id+"F0.wireOp",EDGE,"d21323fb-2d8b-4c74-bdcf-1873a6e3dc00");Q2=makeQuery(id+"F0.imprint","IMPRINT",FACE,{"disambiguationData":[TD([[makeQuery(id+"F0.imprint","IMPRINT",EDGE,{"derivedFrom":subQ1}),-1.0]])]});}
            var Q3;
            {var subQ2=sQuery(id+"F0.wireOp",EDGE,"E49");Q3=makeQuery(id+"F0.imprint","IMPRINT",FACE,{"disambiguationData":[TD([[makeQuery(id+"F0.imprint","IMPRINT",EDGE,{"derivedFrom":subQ2}),-1.0]])]});}
            extrude(context, id + "F5", {"entities" : qUnion([Q0, Q1, Q2, Q3]), "operationType" : NewBodyOperationType.ADD, "depth" : 4 * mm});
        }
        {
            var Q0;
            Q0=makeQuery(id+"F0.imprint","IMPRINT",FACE,{"disambiguationData":[TD([[makeQuery(id+"F0.imprint","IMPRINT",EDGE,{"derivedFrom":sQuery(id+"F0.wireOp",EDGE,"E43")}),-1.0]])]});
            extrude(context, id + "F6", {"entities" : qUnion([Q0]), "operationType" : NewBodyOperationType.ADD, "depth" : 21 * mm, "hasSecondDirection" : true, "secondDirectionOppositeDirection" : false, "secondDirectionDepth" : 20 * mm});
        }
        {
            var Q0;
            Q0=makeQuery(id+"F0.imprint","IMPRINT",FACE,{"disambiguationData":[TD([[makeQuery(id+"F0.imprint","IMPRINT",EDGE,{"derivedFrom":sQuery(id+"F0.wireOp",EDGE,"E84")}),-1.0]])]});
            extrude(context, id + "F7", {"entities" : qUnion([Q0]), "depth" : 5 * mm});
        }
        {
            var Q0;
            Q0=makeQuery(id+"F6.opExtrude","CAP_EDGE",EDGE,{"disambiguationData":[OSD([sQuery(id+"F0.wireOp",EDGE,"E43")])],"isStart":true});
            chamfer(context, id + "F8", {"entities" : qUnion([Q0]), "width" : 0.5 * mm, "tangentPropagation" : true});
        }
        {
            var Q0;
            {var subQ16=sQuery(id+"F0.wireOp",EDGE,"E152");Q0=makeQuery(id+"F0.imprint","IMPRINT",FACE,{"disambiguationData":[TD([[makeQuery(id+"F0.imprint","IMPRINT",EDGE,{"derivedFrom":subQ16}),1.0]])]});}
            extrude(context, id + "F9", {"entities" : qUnion([Q0]), "depth" : 25 * mm});
        }
        {
            var Q0;
            Q0=makeQuery(id+"F0.imprint","IMPRINT",FACE,{"disambiguationData":[TD([[makeQuery(id+"F0.imprint","IMPRINT",EDGE,{"derivedFrom":sQuery(id+"F0.wireOp",EDGE,"E154.MirrorC")}),1.0]])]});
            var Q1;
            Q1=makeQuery(id+"F0.imprint","IMPRINT",FACE,{"disambiguationData":[TD([[makeQuery(id+"F0.imprint","IMPRINT",EDGE,{"derivedFrom":sQuery(id+"F0.wireOp",EDGE,"E155.MirrorC")}),1.0]])]});
            var Q2;
            Q2=makeQuery(id+"F0.imprint","IMPRINT",FACE,{"disambiguationData":[TD([[makeQuery(id+"F0.imprint","IMPRINT",EDGE,{"derivedFrom":sQuery(id+"F0.wireOp",EDGE,"E204")}),-1.0]])]});
            var Q3;
            {var subQ0=sQuery(id+"F0.wireOp",EDGE,"E148");var subQ1=sQuery(id+"F0.wireOp",EDGE,"E144");var subQ2=makeQuery(id+"F0.imprint","INTERSECT",VERTEX,{"disambiguationData":[OD(0.0)],"derivedFrom":[subQ1,subQ0]});Q3=makeQuery(id+"F0.imprint","IMPRINT",FACE,{"disambiguationData":[TD([[makeQuery(id+"F0.imprint","IMPRINT",EDGE,{"disambiguationData":[TD([[subQ2,-1.0]])],"derivedFrom":subQ1}),1.0]])]});}
            var Q4;
            {var subQ0=sQuery(id+"F0.wireOp",EDGE,"E149");var subQ1=sQuery(id+"F0.wireOp",EDGE,"E144");var subQ2=makeQuery(id+"F0.imprint","INTERSECT",VERTEX,{"disambiguationData":[OD(0.0)],"derivedFrom":[subQ1,subQ0]});Q4=makeQuery(id+"F0.imprint","IMPRINT",FACE,{"disambiguationData":[TD([[makeQuery(id+"F0.imprint","IMPRINT",EDGE,{"disambiguationData":[TD([[subQ2,1.0]])],"derivedFrom":subQ1}),1.0]])]});}
            extrude(context, id + "F10", {"entities" : qUnion([Q0, Q1, Q2, Q3, Q4]), "operationType" : NewBodyOperationType.ADD, "depth" : 4 * mm});
        }
        {
            var Q0;
            Q0=makeQuery(id+"F5.opExtrude","CAP_EDGE",EDGE,{"disambiguationData":[OSD([sQuery(id+"F0.wireOp",EDGE,"E58.left")])],"isStart":false});
            var Q1;
            Q1=makeQuery(id+"F5.opExtrude","CAP_EDGE",EDGE,{"disambiguationData":[OSD([sQuery(id+"F0.wireOp",EDGE,"E64.filletArc")])],"isStart":false});
            var Q2;
            Q2=makeQuery(id+"F5.opExtrude","CAP_EDGE",EDGE,{"disambiguationData":[OSD([sQuery(id+"F0.wireOp",EDGE,"E49")])],"isStart":false});
            var Q3;
            Q3=makeQuery(id+"F5.opExtrude","CAP_EDGE",EDGE,{"disambiguationData":[OSD([sQuery(id+"F0.wireOp",EDGE,"E68.trimOffspring")])],"isStart":false});
            var Q4;
            Q4=makeQuery(id+"F9.opExtrude","CAP_EDGE",EDGE,{"disambiguationData":[OSD([sQuery(id+"F0.wireOp",EDGE,"E158.left")])],"isStart":false});
            var Q5;
            Q5=makeQuery(id+"F9.opExtrude","CAP_EDGE",EDGE,{"disambiguationData":[OSD([sQuery(id+"F0.wireOp",EDGE,"E168.trimOffspring")])],"isStart":false});
            var Q6;
            Q6=makeQuery(id+"F9.opExtrude","CAP_EDGE",EDGE,{"disambiguationData":[OSD([sQuery(id+"F0.wireOp",EDGE,"E144")])],"isStart":false});
            var Q7;
            Q7=makeQuery(id+"F10.opExtrude","CAP_EDGE",EDGE,{"disambiguationData":[OSD([sQuery(id+"F0.wireOp",EDGE,"E158.left")])],"isStart":false});
            var Q8;
            Q8=makeQuery(id+"F10.opExtrude","CAP_EDGE",EDGE,{"disambiguationData":[OSD([sQuery(id+"F0.wireOp",EDGE,"E167.trimOffspring")])],"isStart":false});
            var Q9;
            Q9=makeQuery(id+"F10.opExtrude","CAP_EDGE",EDGE,{"disambiguationData":[OSD([sQuery(id+"F0.wireOp",EDGE,"E157.top")])],"isStart":false});
            var Q10;
            Q10=makeQuery(id+"F10.opExtrude","CAP_EDGE",EDGE,{"disambiguationData":[OSD([sQuery(id+"F0.wireOp",EDGE,"E168.trimOffspring")])],"isStart":false});
            fillet(context, id + "F11", {"entities" : qUnion([Q0, Q1, Q2, Q3, Q4, Q5, Q6, Q7, Q8, Q9, Q10]), "radius" : 5 * mm, "tangentPropagation" : true, "allowEdgeOverflow" : false});
        }
        {
            var Q0;
            Q0=makeQuery(id+"F4.opExtrude","CAP_EDGE",EDGE,{"disambiguationData":[OSD([sQuery(id+"F0.wireOp",EDGE,"E49")])],"isStart":false});
            var Q1;
            Q1=makeQuery(id+"F5.opExtrude","CAP_EDGE",EDGE,{"disambiguationData":[OSD([sQuery(id+"F0.wireOp",EDGE,"E51")])],"isStart":false});
            var Q2;
            Q2=makeQuery(id+"F5.opExtrude","CAP_EDGE",EDGE,{"disambiguationData":[OSD([sQuery(id+"F0.wireOp",EDGE,"E46")])],"isStart":false});
            var Q3;
            Q3=makeQuery(id+"F5.opExtrude","CAP_EDGE",EDGE,{"disambiguationData":[OSD([sQuery(id+"F0.wireOp",EDGE,"E53")])],"isStart":false});
            var Q4;
            Q4=makeQuery(id+"F5.opExtrude","CAP_EDGE",EDGE,{"disambiguationData":[OSD([sQuery(id+"F0.wireOp",EDGE,"E47")])],"isStart":false});
            var Q5;
            Q5=makeQuery(id+"F10.opExtrude","CAP_EDGE",EDGE,{"disambiguationData":[OSD([sQuery(id+"F0.wireOp",EDGE,"E149")])],"isStart":false});
            var Q6;
            Q6=makeQuery(id+"F10.opExtrude","CAP_EDGE",EDGE,{"disambiguationData":[OSD([sQuery(id+"F0.wireOp",EDGE,"E148")])],"isStart":false});
            var Q7;
            Q7=makeQuery(id+"F10.opExtrude","CAP_EDGE",EDGE,{"disambiguationData":[OSD([sQuery(id+"F0.wireOp",EDGE,"E153")])],"isStart":false});
            var Q8;
            Q8=makeQuery(id+"F9.opExtrude","SWEPT_EDGE",EDGE,{"disambiguationData":[OSD([sQuery(id+"F0.wireOp",EDGE,"E153"),sQuery(id+"F0.wireOp",EDGE,"E158.left")])]});
            var Q9;
            Q9=makeQuery(id+"F10.opExtrude","CAP_EDGE",EDGE,{"disambiguationData":[OSD([sQuery(id+"F0.wireOp",EDGE,"E151")])],"isStart":false});
            var Q10;
            {var subQ0=sQuery(id+"F0.wireOp",EDGE,"E151");Q10=makeQuery(id+"F11.opFillet","BLEND_EDGE",EDGE,{"blendedFrom":[makeQuery(id+"F10.opExtrude","CAP_EDGE",EDGE,{"disambiguationData":[OSD([sQuery(id+"F0.wireOp",EDGE,"E168.trimOffspring")])],"isStart":false}),makeQuery(id+"F10.boolean.opBoolean","MERGE",FACE,{"derivedFrom":[makeQuery(id+"F9.opExtrude","SWEPT_FACE",FACE,{"disambiguationData":[OSD([subQ0])]}),makeQuery(id+"F10.opExtrude","SWEPT_FACE",FACE,{"disambiguationData":[OSD([subQ0])]})]})],"blendedInto":[makeQuery(id+"F10.boolean.opBoolean","MERGE",FACE,{"derivedFrom":[makeQuery(id+"F9.opExtrude","SWEPT_FACE",FACE,{"disambiguationData":[OSD([subQ0])]}),makeQuery(id+"F10.opExtrude","SWEPT_FACE",FACE,{"disambiguationData":[OSD([subQ0])]})]})]});}
            fillet(context, id + "F12", {"entities" : qUnion([Q0, Q1, Q2, Q3, Q4, Q5, Q6, Q7, Q8, Q9, Q10]), "radius" : 3 * mm, "tangentPropagation" : true, "allowEdgeOverflow" : false});
        }
        {
            var Q0;
            Q0=makeQuery(id+"F0.imprint","IMPRINT",FACE,{"disambiguationData":[TD([[makeQuery(id+"F0.imprint","IMPRINT",EDGE,{"derivedFrom":sQuery(id+"F0.wireOp",EDGE,"f4d605e5-f8c4-4358-9a59-65ac05495e07")}),-1.0]])]});
            var Q1;
            {var subQ1=sQuery(id+"F0.wireOp",EDGE,"c733202e-df79-4c57-a5cb-e2746a1ac155");Q1=makeQuery(id+"F0.imprint","IMPRINT",FACE,{"disambiguationData":[TD([[makeQuery(id+"F0.imprint","IMPRINT",EDGE,{"derivedFrom":subQ1}),-1.0]])]});}
            var Q2;
            Q2=makeQuery(id+"F0.imprint","IMPRINT",FACE,{"disambiguationData":[TD([[makeQuery(id+"F0.imprint","IMPRINT",EDGE,{"derivedFrom":sQuery(id+"F0.wireOp",EDGE,"E21")}),1.0]])]});
            var Q3;
            Q3=makeQuery(id+"F0.imprint","IMPRINT",FACE,{"disambiguationData":[TD([[makeQuery(id+"F0.imprint","IMPRINT",EDGE,{"derivedFrom":sQuery(id+"F0.wireOp",EDGE,"E18")}),-1.0]])]});
            var Q4;
            Q4=makeQuery(id+"F0.imprint","IMPRINT",FACE,{"disambiguationData":[TD([[makeQuery(id+"F0.imprint","IMPRINT",EDGE,{"derivedFrom":sQuery(id+"F0.wireOp",EDGE,"E18")}),1.0]])]});
            extrude(context, id + "F13", {"entities" : qUnion([Q0, Q1, Q2, Q3, Q4]), "depth" : 4 * mm});
        }
        {
            var Q0;
            Q0=makeQuery(id+"F3.opExtrude","SWEPT_BODY",BODY,{"disambiguationData":[OSD([sQuery(id+"F0.wireOp",EDGE,"E21"),sQuery(id+"F0.wireOp",EDGE,"E22"),sQuery(id+"F0.wireOp",EDGE,"E28"),sQuery(id+"F0.wireOp",EDGE,"E29"),sQuery(id+"F0.wireOp",EDGE,"E30"),sQuery(id+"F0.wireOp",EDGE,"E31"),sQuery(id+"F0.wireOp",EDGE,"E32"),sQuery(id+"F0.wireOp",EDGE,"E33"),sQuery(id+"F0.wireOp",EDGE,"E36"),sQuery(id+"F0.wireOp",EDGE,"E37"),sQuery(id+"F0.wireOp",EDGE,"E38"),sQuery(id+"F0.wireOp",EDGE,"E39"),sQuery(id+"F0.wireOp",EDGE,"E40.MirrorC"),sQuery(id+"F0.wireOp",EDGE,"E41.MirrorC")])]});
            transform(context, id + "F14", {"entities" : qUnion([Q0]), "transformType" : TransformType.TRANSLATION_3D, "dx" : 0 * mm, "dy" : 63.6 * mm, "dz" : 0 * mm, "makeCopy" : false});
        }
        {
            var Q0;
            Q0=makeQuery(id+"F4.opExtrude","SWEPT_BODY",BODY,{"disambiguationData":[OSD([sQuery(id+"F0.wireOp",EDGE,"E49"),sQuery(id+"F0.wireOp",EDGE,"E51"),sQuery(id+"F0.wireOp",EDGE,"E52"),sQuery(id+"F0.wireOp",EDGE,"E53"),sQuery(id+"F0.wireOp",EDGE,"E56.0"),sQuery(id+"F0.wireOp",EDGE,"E56.1"),sQuery(id+"F0.wireOp",EDGE,"E56.2"),sQuery(id+"F0.wireOp",EDGE,"E56.3"),sQuery(id+"F0.wireOp",EDGE,"E56.4"),sQuery(id+"F0.wireOp",EDGE,"E56.5"),sQuery(id+"F0.wireOp",EDGE,"E57.top"),sQuery(id+"F0.wireOp",EDGE,"E58.left"),sQuery(id+"F0.wireOp",EDGE,"E63.filletArc"),sQuery(id+"F0.wireOp",EDGE,"E64.filletArc"),sQuery(id+"F0.wireOp",EDGE,"E65"),sQuery(id+"F0.wireOp",EDGE,"E66"),sQuery(id+"F0.wireOp",EDGE,"E67.trimOffspring"),sQuery(id+"F0.wireOp",EDGE,"E68.trimOffspring"),sQuery(id+"F0.wireOp",EDGE,"E110"),sQuery(id+"F0.wireOp",EDGE,"E116"),sQuery(id+"F0.wireOp",EDGE,"E117.trimOffspring"),sQuery(id+"F0.wireOp",EDGE,"E120.MirrorCS"),sQuery(id+"F0.wireOp",EDGE,"E127.trimOffspring"),sQuery(id+"F0.wireOp",EDGE,"E128.0"),sQuery(id+"F0.wireOp",EDGE,"E128.1"),sQuery(id+"F0.wireOp",EDGE,"E128.2"),sQuery(id+"F0.wireOp",EDGE,"E130.MirrorCS"),sQuery(id+"F0.wireOp",EDGE,"E131.MirrorCS"),sQuery(id+"F0.wireOp",EDGE,"E132.MirrorCS"),sQuery(id+"F0.wireOp",EDGE,"E133"),sQuery(id+"F0.wireOp",EDGE,"E134"),sQuery(id+"F0.wireOp",EDGE,"E135"),sQuery(id+"F0.wireOp",EDGE,"E137.0"),sQuery(id+"F0.wireOp",EDGE,"E137.1"),sQuery(id+"F0.wireOp",EDGE,"E137.2"),sQuery(id+"F0.wireOp",EDGE,"E138.MirrorCS"),sQuery(id+"F0.wireOp",EDGE,"E139.MirrorCS"),sQuery(id+"F0.wireOp",EDGE,"E140.MirrorCS"),sQuery(id+"F0.wireOp",EDGE,"E141"),sQuery(id+"F0.wireOp",EDGE,"E142"),sQuery(id+"F0.wireOp",EDGE,"E143")])]});
            transform(context, id + "F15", {"entities" : qUnion([Q0]), "transformType" : TransformType.TRANSLATION_3D, "dx" : -16 * mm, "dy" : 109 * mm, "dz" : 0 * mm, "makeCopy" : false});
        }
        {
            var Q0;
            Q0=makeQuery(id+"F0.imprint","IMPRINT",FACE,{"disambiguationData":[TD([[makeQuery(id+"F0.imprint","IMPRINT",EDGE,{"derivedFrom":sQuery(id+"F0.wireOp",EDGE,"f4d605e5-f8c4-4358-9a59-65ac05495e07")}),-1.0]])]});
            var Q1;
            Q1=makeQuery(id+"F0.imprint","IMPRINT",FACE,{"disambiguationData":[TD([[makeQuery(id+"F0.imprint","IMPRINT",EDGE,{"derivedFrom":sQuery(id+"F0.wireOp",EDGE,"E21")}),1.0]])]});
            var Q2;
            {var subQ1=sQuery(id+"F0.wireOp",EDGE,"c733202e-df79-4c57-a5cb-e2746a1ac155");Q2=makeQuery(id+"F0.imprint","IMPRINT",FACE,{"disambiguationData":[TD([[makeQuery(id+"F0.imprint","IMPRINT",EDGE,{"derivedFrom":subQ1}),-1.0]])]});}
            extrude(context, id + "F16", {"entities" : qUnion([Q0, Q1, Q2]), "depth" : 4 * mm});
        }
        {
            var Q0;
            Q0=makeQuery(id+"F16.opExtrude","SWEPT_BODY",BODY,{"disambiguationData":[OSD([sQuery(id+"F0.wireOp",EDGE,"E21"),sQuery(id+"F0.wireOp",EDGE,"E22"),sQuery(id+"F0.wireOp",EDGE,"E28"),sQuery(id+"F0.wireOp",EDGE,"E29"),sQuery(id+"F0.wireOp",EDGE,"E31"),sQuery(id+"F0.wireOp",EDGE,"E32"),sQuery(id+"F0.wireOp",EDGE,"E33"),sQuery(id+"F0.wireOp",EDGE,"E36"),sQuery(id+"F0.wireOp",EDGE,"E37"),sQuery(id+"F0.wireOp",EDGE,"E38"),sQuery(id+"F0.wireOp",EDGE,"E39"),sQuery(id+"F0.wireOp",EDGE,"E40.MirrorC"),sQuery(id+"F0.wireOp",EDGE,"E41.MirrorC"),sQuery(id+"F0.wireOp",EDGE,"E256")])]});
            transform(context, id + "F17", {"entities" : qUnion([Q0]), "transformType" : TransformType.TRANSLATION_3D, "dx" : 0 * mm, "dy" : -93.8 * mm, "dz" : 0 * mm, "makeCopy" : false});
        }
        {
            var Q0;
            Q0=makeQuery(id+"F13.opExtrude","SWEPT_BODY",BODY,{"disambiguationData":[OSD([sQuery(id+"F0.wireOp",EDGE,"E21"),sQuery(id+"F0.wireOp",EDGE,"E22"),sQuery(id+"F0.wireOp",EDGE,"E28"),sQuery(id+"F0.wireOp",EDGE,"E29"),sQuery(id+"F0.wireOp",EDGE,"E31"),sQuery(id+"F0.wireOp",EDGE,"E32"),sQuery(id+"F0.wireOp",EDGE,"E33"),sQuery(id+"F0.wireOp",EDGE,"E36"),sQuery(id+"F0.wireOp",EDGE,"E37"),sQuery(id+"F0.wireOp",EDGE,"E38"),sQuery(id+"F0.wireOp",EDGE,"E39"),sQuery(id+"F0.wireOp",EDGE,"E40.MirrorC"),sQuery(id+"F0.wireOp",EDGE,"E41.MirrorC"),sQuery(id+"F0.wireOp",EDGE,"E255")])]});
            transform(context, id + "F18", {"entities" : qUnion([Q0]), "transformType" : TransformType.TRANSLATION_3D, "dx" : 0 * mm, "dy" : -164.3 * mm, "dz" : 0 * mm, "makeCopy" : false});
        }
        {
            var Q0;
            Q0=makeQuery(id+"F9.opExtrude","SWEPT_BODY",BODY,{"disambiguationData":[OSD([sQuery(id+"F0.wireOp",EDGE,"E144"),sQuery(id+"F0.wireOp",EDGE,"E151"),sQuery(id+"F0.wireOp",EDGE,"E152"),sQuery(id+"F0.wireOp",EDGE,"E153"),sQuery(id+"F0.wireOp",EDGE,"E157.top"),sQuery(id+"F0.wireOp",EDGE,"E158.left"),sQuery(id+"F0.wireOp",EDGE,"E165"),sQuery(id+"F0.wireOp",EDGE,"E166"),sQuery(id+"F0.wireOp",EDGE,"E167.trimOffspring"),sQuery(id+"F0.wireOp",EDGE,"E168.trimOffspring"),sQuery(id+"F0.wireOp",EDGE,"E169"),sQuery(id+"F0.wireOp",EDGE,"E175"),sQuery(id+"F0.wireOp",EDGE,"E176.trimOffspring"),sQuery(id+"F0.wireOp",EDGE,"E179.MirrorCS"),sQuery(id+"F0.wireOp",EDGE,"E186.trimOffspring"),sQuery(id+"F0.wireOp",EDGE,"E187.0"),sQuery(id+"F0.wireOp",EDGE,"E187.1"),sQuery(id+"F0.wireOp",EDGE,"E187.2"),sQuery(id+"F0.wireOp",EDGE,"E189.MirrorCS"),sQuery(id+"F0.wireOp",EDGE,"E190.MirrorCS"),sQuery(id+"F0.wireOp",EDGE,"E191.MirrorCS"),sQuery(id+"F0.wireOp",EDGE,"E192"),sQuery(id+"F0.wireOp",EDGE,"E193"),sQuery(id+"F0.wireOp",EDGE,"E194"),sQuery(id+"F0.wireOp",EDGE,"E196.0"),sQuery(id+"F0.wireOp",EDGE,"E196.1"),sQuery(id+"F0.wireOp",EDGE,"E196.2"),sQuery(id+"F0.wireOp",EDGE,"E197.MirrorCS"),sQuery(id+"F0.wireOp",EDGE,"E198.MirrorCS"),sQuery(id+"F0.wireOp",EDGE,"E199.MirrorCS"),sQuery(id+"F0.wireOp",EDGE,"E200"),sQuery(id+"F0.wireOp",EDGE,"E201"),sQuery(id+"F0.wireOp",EDGE,"E202")])]});
            transform(context, id + "F19", {"entities" : qUnion([Q0]), "transformType" : TransformType.TRANSLATION_3D, "dx" : -93 * mm, "dy" : -54 * mm, "dz" : 0 * mm, "makeCopy" : false});
        }
    });
